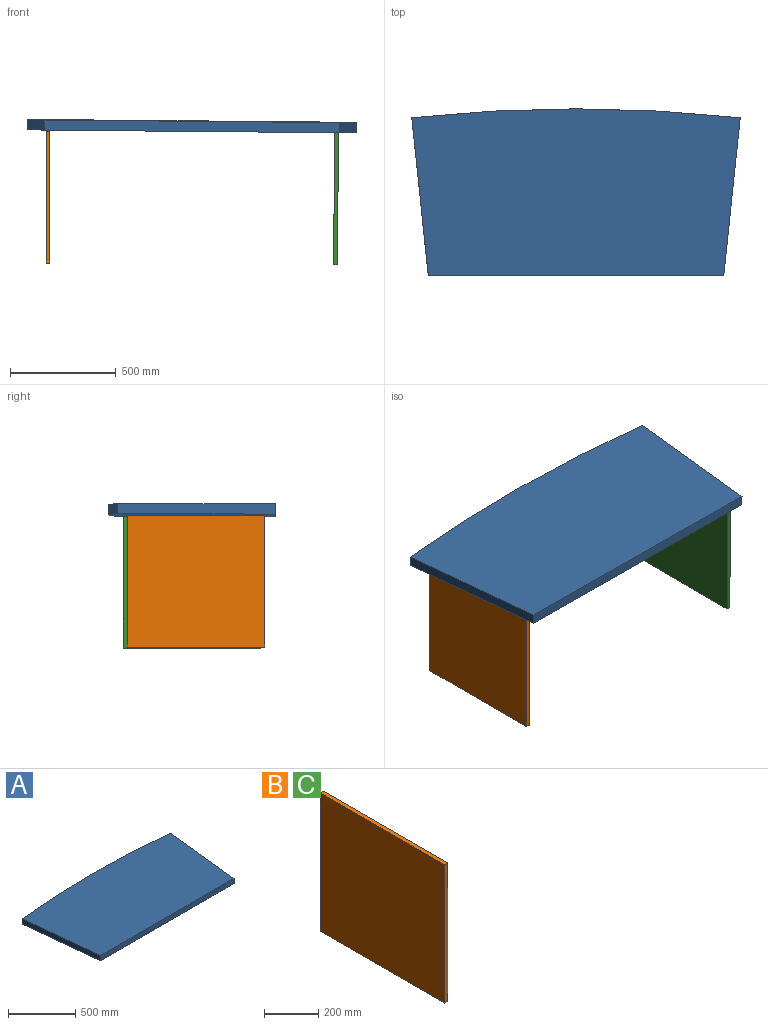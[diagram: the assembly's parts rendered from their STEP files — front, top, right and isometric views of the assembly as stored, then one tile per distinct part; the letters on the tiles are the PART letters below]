
ASSEMBLY  parts=3 mates=1
PART A: 6 faces, bbox 1556.8x788.2x48 mm
  f0: plane 745.89x78.4mm, normal (0.99,-0.1,0), area 36000mm2, adj f1,f3,f4,f5
  f1: cylinder r=7179mm len=1556.79mm, axis (0,0,-1), area 74873.2mm2, adj f0,f2,f4,f5
  f2: plane 745.89x78.4mm, normal (-0.99,-0.1,0), area 36000mm2, adj f1,f3,f4,f5
  f3: plane 1400x48mm, normal (0,-1,0), area 67200mm2, adj f0,f2,f4,f5
  f4: plane 1556.79x788.22mm, normal (0,0,1), area 1146675.9mm2, adj f0,f1,f2,f3
  f5: plane 1556.79x788.22mm, normal (0,0,-1), area 1146675.9mm2, adj f0,f1,f2,f3
PART B: 6 faces, bbox 18x650x625 mm
  f0: plane 625x18mm, normal (0,-1,0), area 11250mm2, adj f1,f3,f4,f5
  f1: plane 650x625mm, normal (1,0,0), area 406250mm2, adj f0,f2,f4,f5
  f2: plane 625x18mm, normal (0,1,0), area 11250mm2, adj f1,f3,f4,f5
  f3: plane 650x625mm, normal (-1,0,0), area 406250mm2, adj f0,f2,f4,f5
  f4: plane 650x18mm, normal (0,0,-1), area 11700mm2, adj f0,f1,f2,f3
  f5: plane 650x18mm, normal (0,0,1), area 11700mm2, adj f0,f1,f2,f3
PART C: same geometry as B
PLACE A rot(axis=(0.28,0.96,0),0.5deg) t=(-236.87,-214.84,161.16)mm
PLACE B t=(-237.75,-214.58,161.35)mm
PLACE C rot(axis=(0.28,0.96,0),0.5deg) t=(1129.59,-195.6,149.13)mm
MATE planar C.f5 <-> A.f5  axis (0.01,0,1) through (480.27,-203.05,154.85)mm
